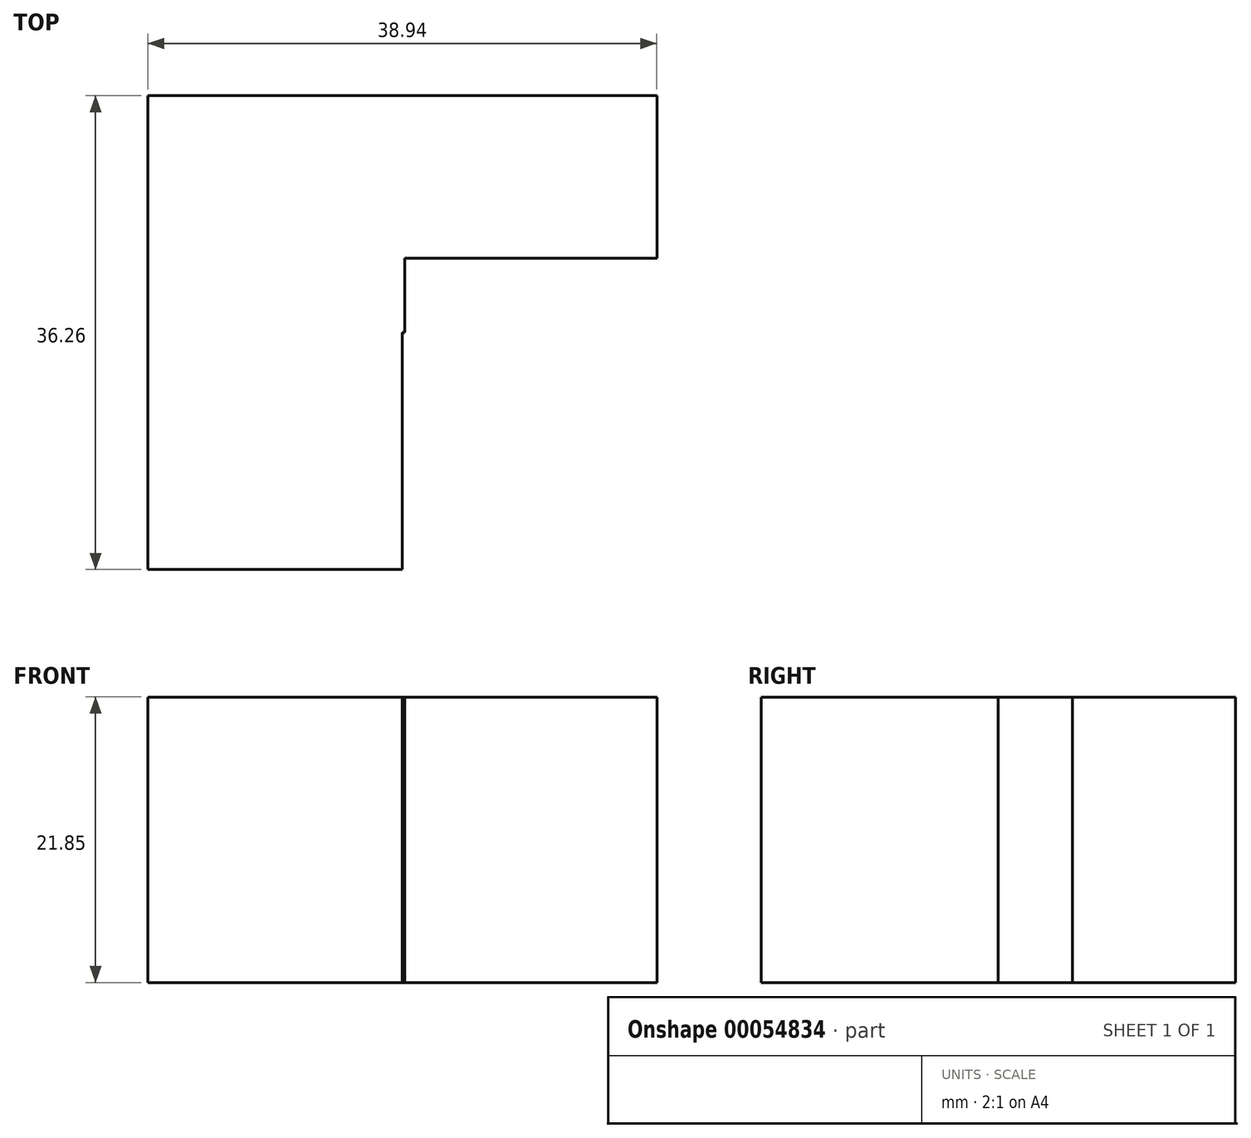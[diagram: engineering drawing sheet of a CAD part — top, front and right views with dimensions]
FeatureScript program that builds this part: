
annotation { "Feature Type Name" : "Feature", "Feature Type Description" : "" }
export const myFeature = defineFeature(function(context is Context, id is Id, definition is map)
    precondition{}
    {
        {
            var Q0;
            Q0=qCreatedBy(makeId("Top.planeOp"),FACE);
            var sketch = newSketch(context, id + "F0", { "sketchPlane" : qUnion([Q0])});
            skLineSegment(sketch, "E0.rect.bottom", {"start": v(0, 0) * mm, "end": v(25.09, 0) * mm});
            skLineSegment(sketch, "E0.rect.top", {"start": v(0, 0) * mm, "end": v(25.09, 0) * mm});
            skLineSegment(sketch, "E0.rect.left", {"start": v(0, 0) * mm, "end": v(0, 0) * mm});
            skLineSegment(sketch, "E0.rect.right", {"start": v(25.09, 0) * mm, "end": v(25.09, 0) * mm});
            skPoint(sketch, "E0.rect.middle", {"position": v(12.54, 0) * mm});
            skLineSegment(sketch, "E1.rect.bottom", {"start": v(22.21, 5.68) * mm, "end": v(0.2, 5.68) * mm});
            skLineSegment(sketch, "E1.rect.top", {"start": v(22.21, -29.08) * mm, "end": v(0.2, -29.08) * mm});
            skLineSegment(sketch, "E1.rect.left", {"start": v(22.21, 5.68) * mm, "end": v(22.21, -29.08) * mm});
            skLineSegment(sketch, "E1.rect.right", {"start": v(0.2, 5.68) * mm, "end": v(0.2, -29.08) * mm});
            skPoint(sketch, "E1.rect.middle", {"position": v(11.2, -11.7) * mm});
            skLineSegment(sketch, "E2.rect.bottom", {"start": v(19.47, 18.13) * mm, "end": v(-19.47, 18.13) * mm});
            skLineSegment(sketch, "E2.rect.top", {"start": v(19.47, -18.13) * mm, "end": v(-19.47, -18.13) * mm});
            skLineSegment(sketch, "E2.rect.left", {"start": v(19.47, 18.13) * mm, "end": v(19.47, -18.13) * mm});
            skLineSegment(sketch, "E2.rect.right", {"start": v(-19.47, 18.13) * mm, "end": v(-19.47, -18.13) * mm});
            skPoint(sketch, "E2.rect.middle", {"position": v(0, 0) * mm});
            skLineSegment(sketch, "E3.bottom", {"start": v(0, 0) * mm, "end": v(41.39, 0) * mm});
            skLineSegment(sketch, "E3.top", {"start": v(0, -20) * mm, "end": v(41.39, -20) * mm});
            skLineSegment(sketch, "E3.left", {"start": v(0, 0) * mm, "end": v(0, -20) * mm});
            skLineSegment(sketch, "E3.right", {"start": v(41.39, 0) * mm, "end": v(41.39, -20) * mm});
            skSolve(sketch);
        }
        {
            var Q0;
            {var subQ9=sQuery(id+"F0.wireOp",EDGE,"E2.rect.bottom");Q0=makeQuery(id+"F0.imprint","IMPRINT",FACE,{"disambiguationData":[TD([[makeQuery(id+"F0.imprint","IMPRINT",EDGE,{"derivedFrom":subQ9}),1.0]])]});}
            extrude(context, id + "F1", {"entities" : qUnion([Q0]), "depth" : 21.85 * mm});
        }
    });
